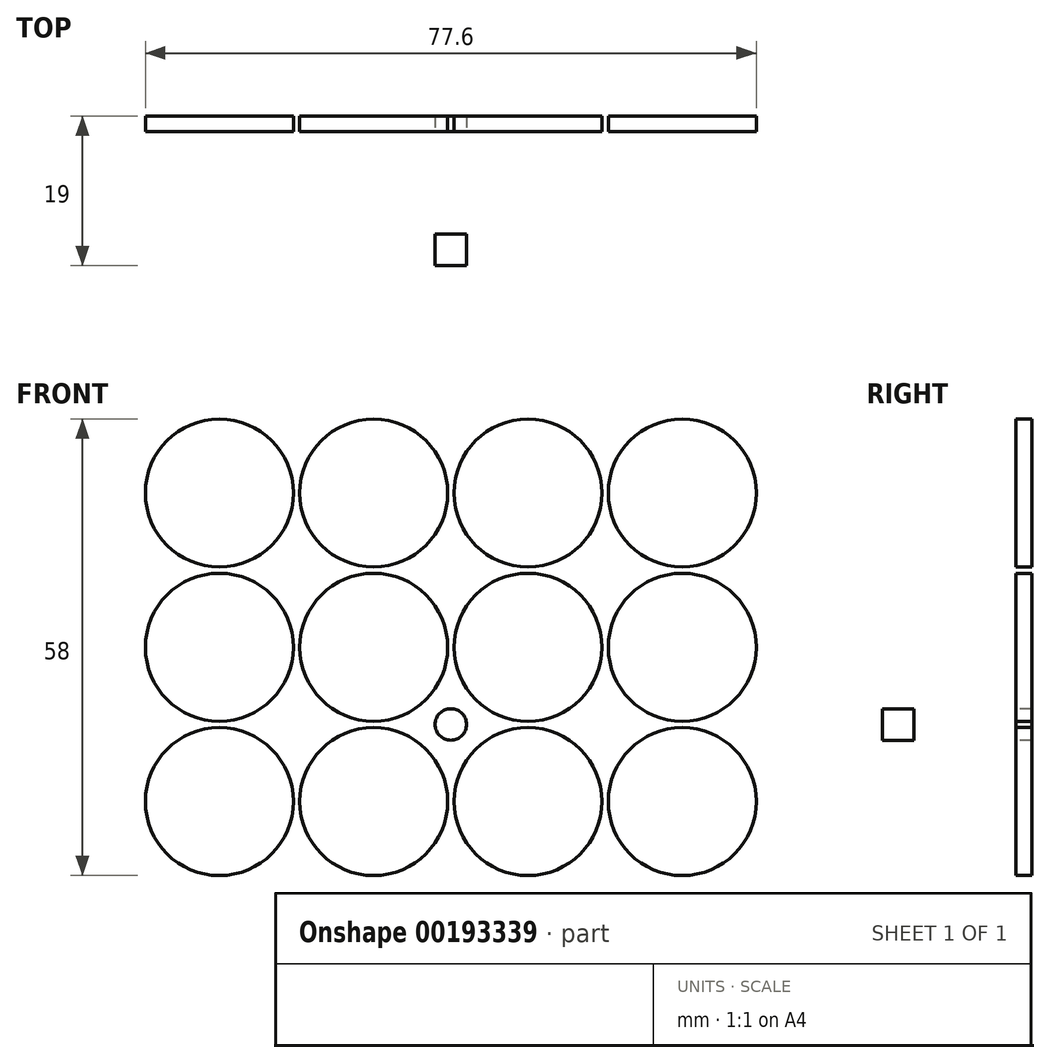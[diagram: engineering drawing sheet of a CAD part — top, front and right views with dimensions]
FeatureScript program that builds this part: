
annotation { "Feature Type Name" : "Feature", "Feature Type Description" : "" }
export const myFeature = defineFeature(function(context is Context, id is Id, definition is map)
    precondition{}
    {
        {
            var Q0;
            Q0=qCreatedBy(makeId("Front.planeOp"),FACE);
            var sketch = newSketch(context, id + "F0", { "sketchPlane" : qUnion([Q0])});
            skCircle(sketch, "E0", {"center": v(0, 0) * mm, "radius": 9.4 * mm});
            skCircle(sketch, "E1.1.0.0", {"center": v(19.6, 0) * mm, "radius": 9.4 * mm});
            skCircle(sketch, "E1.2.0.0", {"center": v(39.2, 0) * mm, "radius": 9.4 * mm});
            skCircle(sketch, "E1.3.0.0", {"center": v(58.8, 0) * mm, "radius": 9.4 * mm});
            skLineSegment(sketch, "E1.direction1", {"start": v(0, 0) * mm, "end": v(19.6, 0) * mm, "construction": true});
            skArc(sketch, "E2", {"start": v(58.8, 9.4) * mm, "mid": v(63.5, 8.14) * mm, "end": v(66.94, 4.7) * mm});
            skArc(sketch, "E3", {"start": v(-8.14, -4.7) * mm, "mid": v(-8.14, 4.7) * mm, "end": v(0, 9.4) * mm});
            skArc(sketch, "E4.0", {"start": v(0, 11.4) * mm, "mid": v(-9.87, 5.7) * mm, "end": v(-9.88, -5.7) * mm});
            skCircle(sketch, "E5.0.1.0", {"center": v(19.6, -19.6) * mm, "radius": 9.4 * mm});
            skCircle(sketch, "E5.0.1.1", {"center": v(39.2, -19.6) * mm, "radius": 9.4 * mm});
            skCircle(sketch, "E5.0.1.2", {"center": v(58.8, -19.6) * mm, "radius": 9.4 * mm});
            skCircle(sketch, "E5.0.1.3", {"center": v(0, -19.6) * mm, "radius": 9.4 * mm});
            skCircle(sketch, "E5.0.2.0", {"center": v(19.6, -39.2) * mm, "radius": 9.4 * mm});
            skCircle(sketch, "E5.0.2.1", {"center": v(39.2, -39.2) * mm, "radius": 9.4 * mm});
            skCircle(sketch, "E5.0.2.2", {"center": v(58.8, -39.2) * mm, "radius": 9.4 * mm});
            skCircle(sketch, "E5.0.2.3", {"center": v(0, -39.2) * mm, "radius": 9.4 * mm});
            skLineSegment(sketch, "E5.direction1", {"start": v(19.6, 0) * mm, "end": v(44.6, 0) * mm, "construction": true});
            skLineSegment(sketch, "E5.direction2", {"start": v(19.6, 0) * mm, "end": v(19.6, -19.6) * mm, "construction": true});
            skArc(sketch, "E6.0", {"start": v(9.8, -45.02) * mm, "mid": v(19.6, -50.6) * mm, "end": v(29.4, -45.02) * mm});
            skArc(sketch, "E7.0", {"start": v(29.4, -45.02) * mm, "mid": v(39.2, -50.6) * mm, "end": v(49, -45.02) * mm});
            skArc(sketch, "E8.0", {"start": v(49, -45.02) * mm, "mid": v(66.86, -47.26) * mm, "end": v(64.62, -29.4) * mm});
            skArc(sketch, "E9.trimOffspring", {"start": v(64.62, -29.4) * mm, "mid": v(70.2, -19.6) * mm, "end": v(64.62, -9.8) * mm});
            skArc(sketch, "E10.trimOffspring", {"start": v(64.62, -9.8) * mm, "mid": v(66.86, 8.06) * mm, "end": v(49, 5.82) * mm});
            skArc(sketch, "E11.trimOffspring", {"start": v(-5.82, -29.4) * mm, "mid": v(-8.06, -47.26) * mm, "end": v(9.8, -45.02) * mm});
            skArc(sketch, "E12.trimOffspring", {"start": v(-5.82, -9.8) * mm, "mid": v(-11.4, -19.6) * mm, "end": v(-5.82, -29.4) * mm});
            skArc(sketch, "E13.trimOffspring", {"start": v(9.8, 5.82) * mm, "mid": v(-8.06, 8.06) * mm, "end": v(-5.82, -9.8) * mm});
            skArc(sketch, "E14.trimOffspring", {"start": v(29.4, 5.82) * mm, "mid": v(19.6, 11.4) * mm, "end": v(9.8, 5.82) * mm});
            skArc(sketch, "E15.trimOffspring", {"start": v(49, 5.82) * mm, "mid": v(39.2, 11.4) * mm, "end": v(29.4, 5.82) * mm});
            skSolve(sketch);
        }
        {
            var Q0;
            Q0=qSketchRegion(id+"F0",true);
            extrude(context, id + "F1", {"entities" : qUnion([Q0]), "depth" : 4 * mm});
        }
        {
            var Q0;
            Q0=makeQuery(id+"F1.opExtrude","CAP_FACE",FACE,{"disambiguationData":[OSD([sQuery(id+"F0.wireOp",EDGE,"E0"),sQuery(id+"F0.wireOp",EDGE,"E1.1.0.0"),sQuery(id+"F0.wireOp",EDGE,"E1.2.0.0"),sQuery(id+"F0.wireOp",EDGE,"E1.3.0.0"),sQuery(id+"F0.wireOp",EDGE,"E5.0.1.0"),sQuery(id+"F0.wireOp",EDGE,"E5.0.1.1"),sQuery(id+"F0.wireOp",EDGE,"E5.0.1.2"),sQuery(id+"F0.wireOp",EDGE,"E5.0.1.3"),sQuery(id+"F0.wireOp",EDGE,"E5.0.2.0"),sQuery(id+"F0.wireOp",EDGE,"E5.0.2.1"),sQuery(id+"F0.wireOp",EDGE,"E5.0.2.2"),sQuery(id+"F0.wireOp",EDGE,"E5.0.2.3"),sQuery(id+"F0.wireOp",EDGE,"E6.0"),sQuery(id+"F0.wireOp",EDGE,"E7.0"),sQuery(id+"F0.wireOp",EDGE,"E8.0"),sQuery(id+"F0.wireOp",EDGE,"E9.trimOffspring"),sQuery(id+"F0.wireOp",EDGE,"E10.trimOffspring"),sQuery(id+"F0.wireOp",EDGE,"E11.trimOffspring"),sQuery(id+"F0.wireOp",EDGE,"E12.trimOffspring"),sQuery(id+"F0.wireOp",EDGE,"E13.trimOffspring"),sQuery(id+"F0.wireOp",EDGE,"E14.trimOffspring"),sQuery(id+"F0.wireOp",EDGE,"E15.trimOffspring")])],"isStart":true});
            var sketch = newSketch(context, id + "F2", { "sketchPlane" : qUnion([Q0])});
            skArc(sketch, "E16.0", {"start": v(5.82, -29.4) * mm, "mid": v(8.06, -47.26) * mm, "end": v(-9.8, -45.02) * mm});
            skArc(sketch, "E16.1", {"start": v(-9.8, -45.02) * mm, "mid": v(-19.6, -50.6) * mm, "end": v(-29.4, -45.02) * mm});
            skArc(sketch, "E16.2", {"start": v(-29.4, -45.02) * mm, "mid": v(-39.2, -50.6) * mm, "end": v(-49, -45.02) * mm});
            skArc(sketch, "E16.3", {"start": v(-49, -45.02) * mm, "mid": v(-66.86, -47.26) * mm, "end": v(-64.62, -29.4) * mm});
            skArc(sketch, "E16.4", {"start": v(5.82, -9.8) * mm, "mid": v(11.4, -19.6) * mm, "end": v(5.82, -29.4) * mm});
            skArc(sketch, "E16.5", {"start": v(-9.8, 5.82) * mm, "mid": v(8.06, 8.06) * mm, "end": v(5.82, -9.8) * mm});
            skArc(sketch, "E16.6", {"start": v(-29.4, 5.82) * mm, "mid": v(-19.6, 11.4) * mm, "end": v(-9.8, 5.82) * mm});
            skArc(sketch, "E16.7", {"start": v(-49, 5.82) * mm, "mid": v(-39.2, 11.4) * mm, "end": v(-29.4, 5.82) * mm});
            skArc(sketch, "E16.8", {"start": v(-64.62, -9.8) * mm, "mid": v(-66.86, 8.06) * mm, "end": v(-49, 5.82) * mm});
            skArc(sketch, "E16.9", {"start": v(-64.62, -29.4) * mm, "mid": v(-70.2, -19.6) * mm, "end": v(-64.62, -9.8) * mm});
            skArc(sketch, "E16.10", {"start": v(-7.32, -45.1) * mm, "mid": v(6.65, -45.85) * mm, "end": v(5.9, -31.88) * mm});
            skArc(sketch, "E16.11", {"start": v(-26.92, -45.1) * mm, "mid": v(-19.6, -48.6) * mm, "end": v(-12.28, -45.1) * mm});
            skArc(sketch, "E16.12", {"start": v(-46.52, -45.1) * mm, "mid": v(-39.2, -48.6) * mm, "end": v(-31.88, -45.1) * mm});
            skArc(sketch, "E16.13", {"start": v(-64.7, -31.88) * mm, "mid": v(-65.45, -45.85) * mm, "end": v(-51.48, -45.1) * mm});
            skArc(sketch, "E16.14", {"start": v(-64.7, -12.28) * mm, "mid": v(-68.2, -19.6) * mm, "end": v(-64.7, -26.92) * mm});
            skArc(sketch, "E16.15", {"start": v(5.9, -26.92) * mm, "mid": v(9.4, -19.6) * mm, "end": v(5.9, -12.28) * mm});
            skArc(sketch, "E16.16", {"start": v(5.9, -7.32) * mm, "mid": v(6.65, 6.65) * mm, "end": v(-7.32, 5.9) * mm});
            skArc(sketch, "E16.17", {"start": v(-12.28, 5.9) * mm, "mid": v(-19.6, 9.4) * mm, "end": v(-26.92, 5.9) * mm});
            skArc(sketch, "E16.18", {"start": v(-31.88, 5.9) * mm, "mid": v(-39.2, 9.4) * mm, "end": v(-46.52, 5.9) * mm});
            skArc(sketch, "E16.19", {"start": v(-51.48, 5.9) * mm, "mid": v(-65.45, 6.65) * mm, "end": v(-64.7, -7.32) * mm});
            skLineSegment(sketch, "E17", {"start": v(-9.8, -45.02) * mm, "end": v(-9.8, -42.02) * mm, "construction": true});
            skLineSegment(sketch, "E18", {"start": v(-9.41, -42.5) * mm, "end": v(-7.32, -45.1) * mm});
            skLineSegment(sketch, "E19.MirrorCS", {"start": v(-10.19, -42.5) * mm, "end": v(-12.28, -45.1) * mm});
            skPoint(sketch, "E20.visualSharp", {"position": v(-9.8, -42.02) * mm});
            skArc(sketch, "E20.filletArc", {"start": v(-9.41, -42.5) * mm, "mid": v(-9.8, -42.32) * mm, "end": v(-10.19, -42.5) * mm});
            skLineSegment(sketch, "E21.1.0.0", {"start": v(-29.01, -42.5) * mm, "end": v(-26.92, -45.1) * mm});
            skArc(sketch, "E21.1.0.1", {"start": v(-29.01, -42.5) * mm, "mid": v(-29.4, -42.32) * mm, "end": v(-29.79, -42.5) * mm});
            skLineSegment(sketch, "E21.1.0.2", {"start": v(-29.79, -42.5) * mm, "end": v(-31.88, -45.1) * mm});
            skLineSegment(sketch, "E21.2.0.0", {"start": v(-48.61, -42.5) * mm, "end": v(-46.52, -45.1) * mm});
            skArc(sketch, "E21.2.0.1", {"start": v(-48.61, -42.5) * mm, "mid": v(-49, -42.32) * mm, "end": v(-49.39, -42.5) * mm});
            skLineSegment(sketch, "E21.2.0.2", {"start": v(-49.39, -42.5) * mm, "end": v(-51.48, -45.1) * mm});
            skLineSegment(sketch, "E21.direction1", {"start": v(-7.32, -45.1) * mm, "end": v(-26.92, -45.1) * mm, "construction": true});
            skLineSegment(sketch, "E22", {"start": v(0, -19.6) * mm, "end": v(-58.8, -19.6) * mm, "construction": true});
            skLineSegment(sketch, "E23.MirrorCS", {"start": v(-9.41, 3.3) * mm, "end": v(-7.32, 5.9) * mm});
            skArc(sketch, "E24.MirrorCS", {"start": v(-9.41, 3.3) * mm, "mid": v(-9.8, 3.12) * mm, "end": v(-10.19, 3.3) * mm});
            skLineSegment(sketch, "E25.MirrorCS", {"start": v(-10.19, 3.3) * mm, "end": v(-12.28, 5.9) * mm});
            skLineSegment(sketch, "E26.MirrorCS", {"start": v(-29.01, 3.3) * mm, "end": v(-26.92, 5.9) * mm});
            skArc(sketch, "E27.MirrorCS", {"start": v(-29.01, 3.3) * mm, "mid": v(-29.4, 3.12) * mm, "end": v(-29.79, 3.3) * mm});
            skLineSegment(sketch, "E28.MirrorCS", {"start": v(-29.79, 3.3) * mm, "end": v(-31.88, 5.9) * mm});
            skLineSegment(sketch, "E29.MirrorCS", {"start": v(-48.61, 3.3) * mm, "end": v(-46.52, 5.9) * mm});
            skArc(sketch, "E30.MirrorCS", {"start": v(-48.61, 3.3) * mm, "mid": v(-49, 3.12) * mm, "end": v(-49.39, 3.3) * mm});
            skLineSegment(sketch, "E31.MirrorCS", {"start": v(-49.39, 3.3) * mm, "end": v(-51.48, 5.9) * mm});
            skLineSegment(sketch, "E32", {"start": v(5.82, -29.4) * mm, "end": v(2.82, -29.4) * mm, "construction": true});
            skLineSegment(sketch, "E33", {"start": v(3.3, -29.79) * mm, "end": v(5.9, -31.88) * mm});
            skLineSegment(sketch, "E34.MirrorCS", {"start": v(3.3, -29.01) * mm, "end": v(5.9, -26.92) * mm});
            skPoint(sketch, "E35.visualSharp", {"position": v(2.82, -29.4) * mm});
            skArc(sketch, "E35.filletArc", {"start": v(3.3, -29.01) * mm, "mid": v(3.12, -29.4) * mm, "end": v(3.3, -29.79) * mm});
            skLineSegment(sketch, "E36.MirrorCS", {"start": v(3.3, -10.19) * mm, "end": v(5.9, -12.28) * mm});
            skLineSegment(sketch, "E37.MirrorCS", {"start": v(3.3, -9.41) * mm, "end": v(5.9, -7.32) * mm});
            skArc(sketch, "E38.MirrorCS", {"start": v(3.3, -10.19) * mm, "mid": v(3.12, -9.8) * mm, "end": v(3.3, -9.41) * mm});
            skLineSegment(sketch, "E39", {"start": v(-29.4, -45.02) * mm, "end": v(-29.4, 5.82) * mm, "construction": true});
            skLineSegment(sketch, "E40.MirrorCS", {"start": v(-62.1, -29.79) * mm, "end": v(-64.7, -31.88) * mm});
            skLineSegment(sketch, "E41.MirrorCS", {"start": v(-62.1, -29.01) * mm, "end": v(-64.7, -26.92) * mm});
            skArc(sketch, "E42.MirrorCS", {"start": v(-62.1, -29.01) * mm, "mid": v(-61.92, -29.4) * mm, "end": v(-62.1, -29.79) * mm});
            skLineSegment(sketch, "E43.MirrorCS", {"start": v(-62.1, -10.19) * mm, "end": v(-64.7, -12.28) * mm});
            skLineSegment(sketch, "E44.MirrorCS", {"start": v(-62.1, -9.41) * mm, "end": v(-64.7, -7.32) * mm});
            skArc(sketch, "E45.MirrorCS", {"start": v(-62.1, -10.19) * mm, "mid": v(-61.92, -9.8) * mm, "end": v(-62.1, -9.41) * mm});
            skSolve(sketch);
        }
        {
            var Q0;
            Q0=makeQuery(id+"F2.imprint","IMPRINT",FACE,{"disambiguationData":[TD([[makeQuery(id+"F2.imprint","IMPRINT",EDGE,{"derivedFrom":sQuery(id+"F2.wireOp",EDGE,"E16.0")}),-1.0]])]});
            extrude(context, id + "F3", {"entities" : qUnion([Q0]), "depth" : 15 * mm});
        }
        {
            var Q0;
            Q0=makeQuery(id+"F3.opExtrude","CAP_FACE",FACE,{"disambiguationData":[OSD([sQuery(id+"F2.wireOp",EDGE,"E16.0"),sQuery(id+"F2.wireOp",EDGE,"E16.1"),sQuery(id+"F2.wireOp",EDGE,"E16.2"),sQuery(id+"F2.wireOp",EDGE,"E16.3"),sQuery(id+"F2.wireOp",EDGE,"E16.4"),sQuery(id+"F2.wireOp",EDGE,"E16.5"),sQuery(id+"F2.wireOp",EDGE,"E16.6"),sQuery(id+"F2.wireOp",EDGE,"E16.7"),sQuery(id+"F2.wireOp",EDGE,"E16.8"),sQuery(id+"F2.wireOp",EDGE,"E16.9"),sQuery(id+"F2.wireOp",EDGE,"E16.10"),sQuery(id+"F2.wireOp",EDGE,"E16.11"),sQuery(id+"F2.wireOp",EDGE,"E16.12"),sQuery(id+"F2.wireOp",EDGE,"E16.13"),sQuery(id+"F2.wireOp",EDGE,"E16.14"),sQuery(id+"F2.wireOp",EDGE,"E16.15"),sQuery(id+"F2.wireOp",EDGE,"E16.16"),sQuery(id+"F2.wireOp",EDGE,"E16.17"),sQuery(id+"F2.wireOp",EDGE,"E16.18"),sQuery(id+"F2.wireOp",EDGE,"E16.19"),sQuery(id+"F2.wireOp",EDGE,"E18"),sQuery(id+"F2.wireOp",EDGE,"E19.MirrorCS"),sQuery(id+"F2.wireOp",EDGE,"E20.filletArc"),sQuery(id+"F2.wireOp",EDGE,"E21.1.0.0"),sQuery(id+"F2.wireOp",EDGE,"E21.1.0.1"),sQuery(id+"F2.wireOp",EDGE,"E21.1.0.2"),sQuery(id+"F2.wireOp",EDGE,"E21.2.0.0"),sQuery(id+"F2.wireOp",EDGE,"E21.2.0.1"),sQuery(id+"F2.wireOp",EDGE,"E21.2.0.2"),sQuery(id+"F2.wireOp",EDGE,"E23.MirrorCS"),sQuery(id+"F2.wireOp",EDGE,"E24.MirrorCS"),sQuery(id+"F2.wireOp",EDGE,"E25.MirrorCS"),sQuery(id+"F2.wireOp",EDGE,"E26.MirrorCS"),sQuery(id+"F2.wireOp",EDGE,"E27.MirrorCS"),sQuery(id+"F2.wireOp",EDGE,"E28.MirrorCS"),sQuery(id+"F2.wireOp",EDGE,"E29.MirrorCS"),sQuery(id+"F2.wireOp",EDGE,"E30.MirrorCS"),sQuery(id+"F2.wireOp",EDGE,"E31.MirrorCS"),sQuery(id+"F2.wireOp",EDGE,"E33"),sQuery(id+"F2.wireOp",EDGE,"E34.MirrorCS"),sQuery(id+"F2.wireOp",EDGE,"E35.filletArc"),sQuery(id+"F2.wireOp",EDGE,"E36.MirrorCS"),sQuery(id+"F2.wireOp",EDGE,"E37.MirrorCS"),sQuery(id+"F2.wireOp",EDGE,"E38.MirrorCS"),sQuery(id+"F2.wireOp",EDGE,"E40.MirrorCS"),sQuery(id+"F2.wireOp",EDGE,"E41.MirrorCS"),sQuery(id+"F2.wireOp",EDGE,"E42.MirrorCS"),sQuery(id+"F2.wireOp",EDGE,"E43.MirrorCS"),sQuery(id+"F2.wireOp",EDGE,"E44.MirrorCS"),sQuery(id+"F2.wireOp",EDGE,"E45.MirrorCS")])],"isStart":false});
            var sketch = newSketch(context, id + "F4", { "sketchPlane" : qUnion([Q0])});
            skArc(sketch, "E46.0", {"start": v(-9.8, -45.02) * mm, "mid": v(-19.6, -50.6) * mm, "end": v(-29.4, -45.02) * mm});
            skArc(sketch, "E46.1", {"start": v(5.82, -29.4) * mm, "mid": v(8.06, -47.26) * mm, "end": v(-9.8, -45.02) * mm});
            skArc(sketch, "E46.2", {"start": v(5.82, -9.8) * mm, "mid": v(11.4, -19.6) * mm, "end": v(5.82, -29.4) * mm});
            skArc(sketch, "E46.3", {"start": v(-9.8, 5.82) * mm, "mid": v(8.06, 8.06) * mm, "end": v(5.82, -9.8) * mm});
            skArc(sketch, "E46.4", {"start": v(-29.4, 5.82) * mm, "mid": v(-19.6, 11.4) * mm, "end": v(-9.8, 5.82) * mm});
            skArc(sketch, "E46.5", {"start": v(-49, 5.82) * mm, "mid": v(-39.2, 11.4) * mm, "end": v(-29.4, 5.82) * mm});
            skArc(sketch, "E46.6", {"start": v(-64.62, -9.8) * mm, "mid": v(-66.86, 8.06) * mm, "end": v(-49, 5.82) * mm});
            skArc(sketch, "E46.7", {"start": v(-64.62, -29.4) * mm, "mid": v(-70.2, -19.6) * mm, "end": v(-64.62, -9.8) * mm});
            skArc(sketch, "E46.8", {"start": v(-49, -45.02) * mm, "mid": v(-66.86, -47.26) * mm, "end": v(-64.62, -29.4) * mm});
            skArc(sketch, "E46.9", {"start": v(-29.4, -45.02) * mm, "mid": v(-39.2, -50.6) * mm, "end": v(-49, -45.02) * mm});
            skSolve(sketch);
        }
        {
            var Q0;
            Q0=makeQuery(id+"F4.imprint","IMPRINT",FACE,{"disambiguationData":[TD([[makeQuery(id+"F4.imprint","IMPRINT",EDGE,{"derivedFrom":makeQuery(id+"F3.opExtrude","CAP_EDGE",EDGE,{"disambiguationData":[OSD([sQuery(id+"F2.wireOp",EDGE,"E16.10")])],"isStart":false})}),-1.0]])]});
            extrude(context, id + "F5", {"entities" : qUnion([Q0]), "operationType" : NewBodyOperationType.ADD, "oppositeDirection" : true, "depth" : 2 * mm});
        }
        {
            var Q0;
            Q0=makeQuery(id+"F1.opExtrude","CAP_FACE",FACE,{"disambiguationData":[OSD([sQuery(id+"F0.wireOp",EDGE,"E0"),sQuery(id+"F0.wireOp",EDGE,"E1.1.0.0"),sQuery(id+"F0.wireOp",EDGE,"E1.2.0.0"),sQuery(id+"F0.wireOp",EDGE,"E1.3.0.0"),sQuery(id+"F0.wireOp",EDGE,"E5.0.1.0"),sQuery(id+"F0.wireOp",EDGE,"E5.0.1.1"),sQuery(id+"F0.wireOp",EDGE,"E5.0.1.2"),sQuery(id+"F0.wireOp",EDGE,"E5.0.1.3"),sQuery(id+"F0.wireOp",EDGE,"E5.0.2.0"),sQuery(id+"F0.wireOp",EDGE,"E5.0.2.1"),sQuery(id+"F0.wireOp",EDGE,"E5.0.2.2"),sQuery(id+"F0.wireOp",EDGE,"E5.0.2.3"),sQuery(id+"F0.wireOp",EDGE,"E6.0"),sQuery(id+"F0.wireOp",EDGE,"E7.0"),sQuery(id+"F0.wireOp",EDGE,"E8.0"),sQuery(id+"F0.wireOp",EDGE,"E9.trimOffspring"),sQuery(id+"F0.wireOp",EDGE,"E10.trimOffspring"),sQuery(id+"F0.wireOp",EDGE,"E11.trimOffspring"),sQuery(id+"F0.wireOp",EDGE,"E12.trimOffspring"),sQuery(id+"F0.wireOp",EDGE,"E13.trimOffspring"),sQuery(id+"F0.wireOp",EDGE,"E14.trimOffspring"),sQuery(id+"F0.wireOp",EDGE,"E15.trimOffspring")])],"isStart":false});
            var sketch = newSketch(context, id + "F6", { "sketchPlane" : qUnion([Q0])});
            skCircle(sketch, "E47.0", {"center": v(19.6, 0) * mm, "radius": 9.4 * mm, "construction": true});
            skCircle(sketch, "E47.1", {"center": v(19.6, -19.6) * mm, "radius": 9.4 * mm, "construction": true});
            skCircle(sketch, "E47.2", {"center": v(39.2, -19.6) * mm, "radius": 9.4 * mm, "construction": true});
            skCircle(sketch, "E47.3", {"center": v(39.2, 0) * mm, "radius": 9.4 * mm, "construction": true});
            skLineSegment(sketch, "E48", {"start": v(19.6, 0) * mm, "end": v(39.2, -19.6) * mm, "construction": true});
            skCircle(sketch, "E49", {"center": v(29.4, -9.8) * mm, "radius": 2 * mm});
            skLineSegment(sketch, "E50", {"start": v(19.6, -19.6) * mm, "end": v(39.2, -19.6) * mm, "construction": true});
            skCircle(sketch, "E51.MirrorC", {"center": v(29.4, -29.4) * mm, "radius": 2 * mm});
            skSolve(sketch);
        }
        {
            var Q0;
            Q0=makeQuery(id+"F6.imprint","IMPRINT",FACE,{"disambiguationData":[TD([[makeQuery(id+"F6.imprint","IMPRINT",EDGE,{"derivedFrom":sQuery(id+"F6.wireOp",EDGE,"E49")}),1.0]])]});
            var Q1;
            Q1=makeQuery(id+"F6.imprint","IMPRINT",FACE,{"disambiguationData":[TD([[makeQuery(id+"F6.imprint","IMPRINT",EDGE,{"derivedFrom":sQuery(id+"F6.wireOp",EDGE,"E51.MirrorC")}),-1.0]])]});
            extrude(context, id + "F7", {"entities" : qUnion([Q0, Q1]), "operationType" : NewBodyOperationType.REMOVE, "endBound" : BoundingType.THROUGH_ALL, "oppositeDirection" : true, "depth" : 25 * mm});
        }
    });
